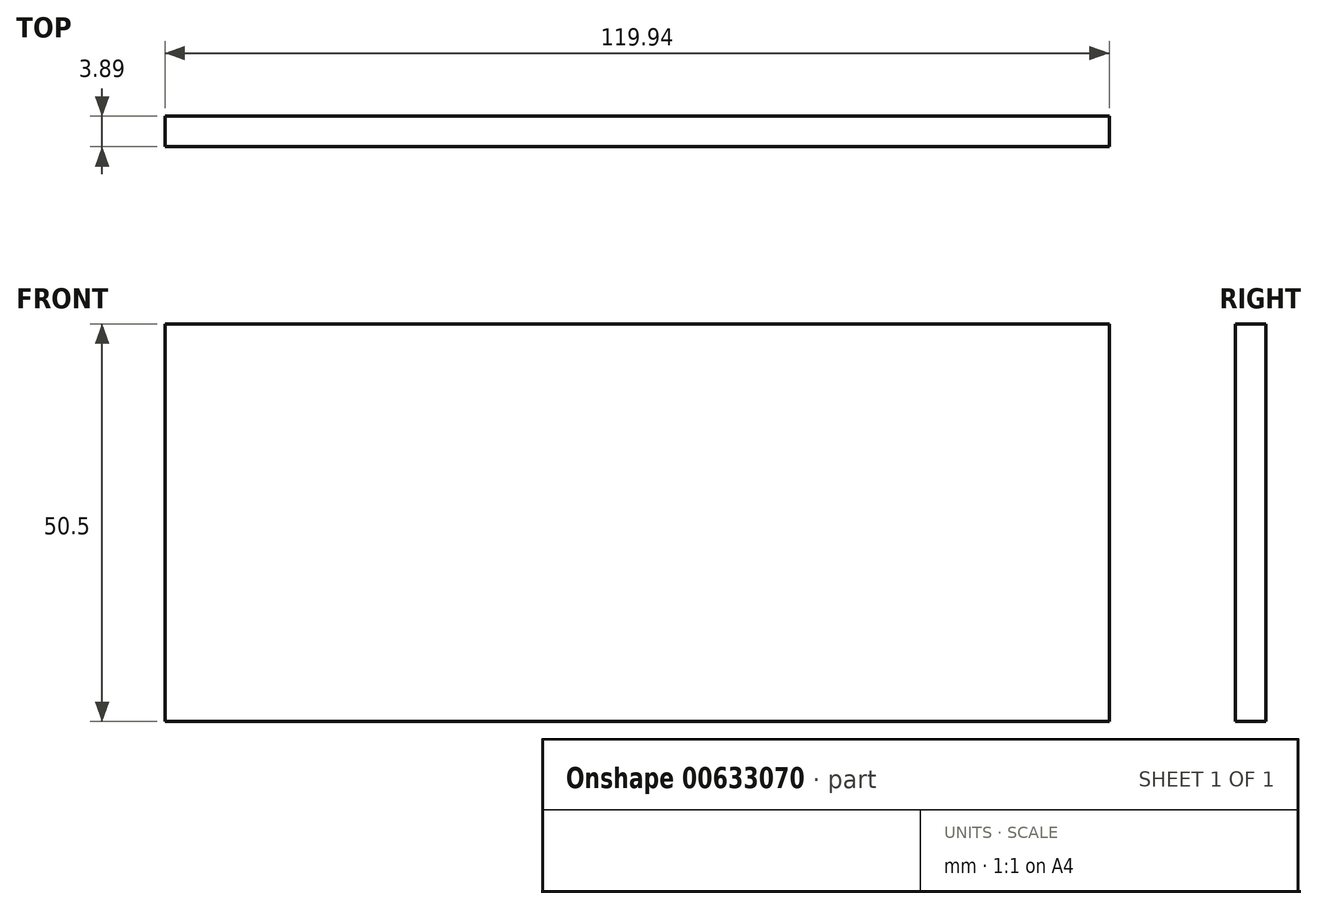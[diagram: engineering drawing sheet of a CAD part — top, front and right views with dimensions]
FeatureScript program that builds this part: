
annotation { "Feature Type Name" : "Feature", "Feature Type Description" : "" }
export const myFeature = defineFeature(function(context is Context, id is Id, definition is map)
    precondition{}
    {
        {
            var Q0;
            Q0=qCreatedBy(makeId("Front.planeOp"),FACE);
            var sketch = newSketch(context, id + "F0", { "sketchPlane" : qUnion([Q0])});
            skLineSegment(sketch, "E0.bottom", {"start": v(-59.97, -25.25) * mm, "end": v(59.97, -25.25) * mm});
            skLineSegment(sketch, "E0.top", {"start": v(-59.97, 25.25) * mm, "end": v(59.97, 25.25) * mm});
            skLineSegment(sketch, "E0.left", {"start": v(-59.97, -25.25) * mm, "end": v(-59.97, 25.25) * mm});
            skLineSegment(sketch, "E0.right", {"start": v(59.97, -25.25) * mm, "end": v(59.97, 25.25) * mm});
            skPoint(sketch, "E0.middle", {"position": v(0, 0) * mm});
            skSolve(sketch);
        }
        {
            var Q0;
            Q0 = qSketchRegion(id + "F0", true);
            extrude(context, id + "F1", {"entities" : qUnion([Q0]), "depth" : 3.9 * mm, "offsetDistance" : 25.4 * mm});
        }
    });
